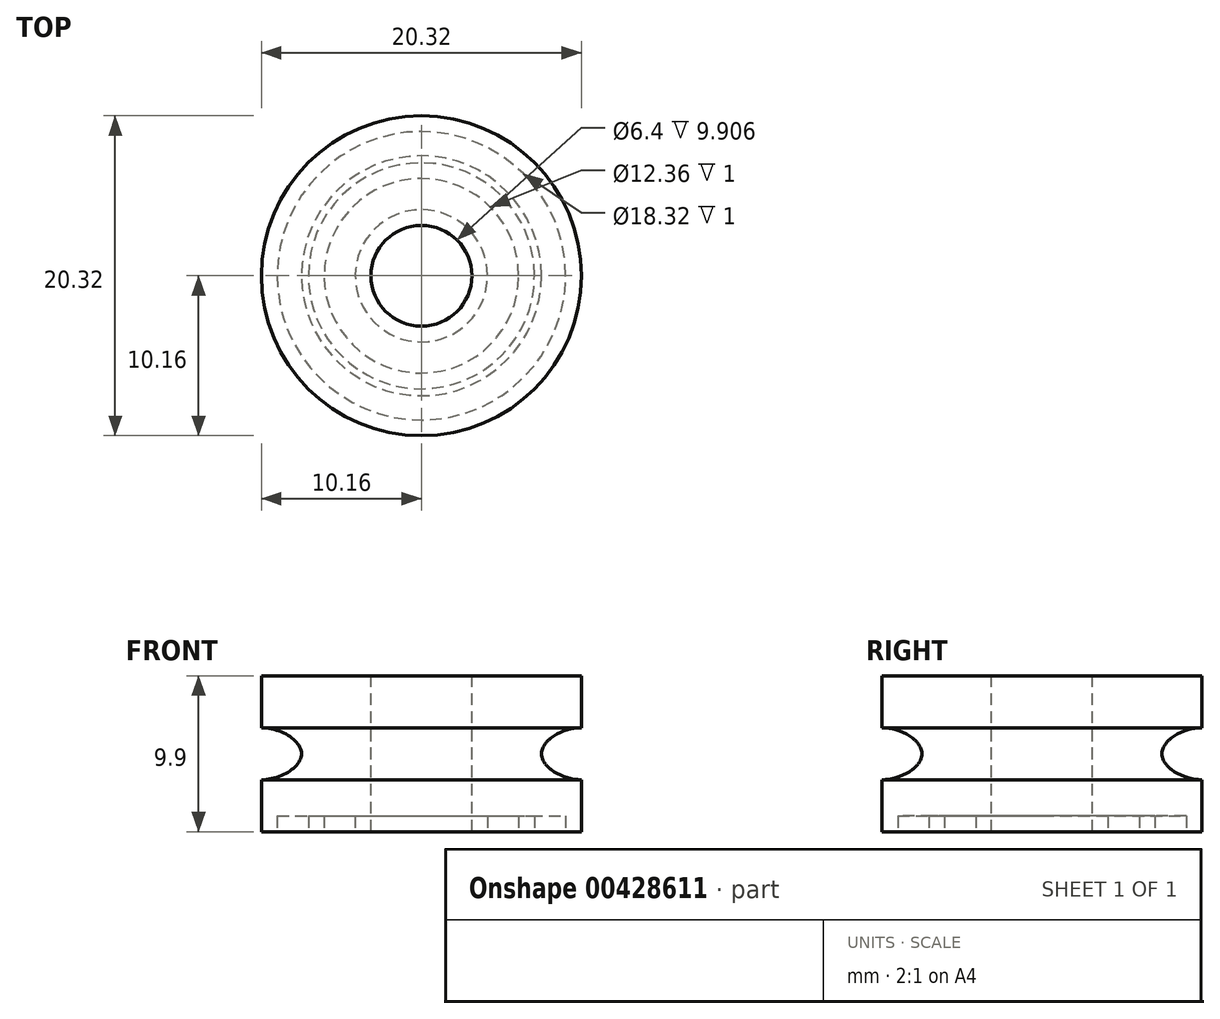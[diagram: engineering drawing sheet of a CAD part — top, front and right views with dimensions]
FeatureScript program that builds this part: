
annotation { "Feature Type Name" : "Feature", "Feature Type Description" : "" }
export const myFeature = defineFeature(function(context is Context, id is Id, definition is map)
    precondition{}
    {
        {
            var Q0;
            Q0=qCreatedBy(makeId("Front.planeOp"),FACE);
            var sketch = newSketch(context, id + "F0", { "sketchPlane" : qUnion([Q0])});
            skLineSegment(sketch, "E0", {"start": v(0, 4.95) * mm, "end": v(-10.16, 4.95) * mm});
            skLineSegment(sketch, "E1", {"start": v(-10.16, 4.95) * mm, "end": v(-10.16, 1.65) * mm});
            skLineSegment(sketch, "E2", {"start": v(-10.16, 1.65) * mm, "end": v(-7.62, 1.65) * mm});
            skLineSegment(sketch, "E3", {"start": v(-7.62, 1.65) * mm, "end": v(-7.62, 0) * mm});
            skLineSegment(sketch, "E4", {"start": v(-7.62, 0) * mm, "end": v(0, 0) * mm});
            skLineSegment(sketch, "E5", {"start": v(0, 0) * mm, "end": v(0, 4.95) * mm});
            skLineSegment(sketch, "E6", {"start": v(0, 0) * mm, "end": v(0, 25.4) * mm, "construction": true});
            skFitSpline(sketch, "E7", {"points": [v(-7.62, 0) * mm, v(-10.16, 1.65) * mm], "startDerivative": vector(0, 2.48) * mm, "endDerivative": vector(-3.81, 0) * mm});
            skSolve(sketch);
        }
        {
            var Q0;
            Q0 = qSketchRegion(id + "F0", true);
            var Q1;
            Q1=sQuery(id+"F0.wireOp",EDGE,"E6");
            revolve(context, id + "F1", {"entities" : qUnion([Q0]), "axis" : qUnion([Q1]), "revolveType" : RevolveType.FULL});
        }
        {
            var Q0;
            Q0=makeQuery(id+"F1.opRevolve","SWEPT_BODY",BODY,{"disambiguationData":[OSD([sQuery(id+"F0.wireOp",EDGE,"E0"),sQuery(id+"F0.wireOp",EDGE,"E1"),sQuery(id+"F0.wireOp",EDGE,"E2"),sQuery(id+"F0.wireOp",EDGE,"E3"),sQuery(id+"F0.wireOp",EDGE,"E4"),sQuery(id+"F0.wireOp",EDGE,"E5")])]});
            var Q1;
            Q1=qCreatedBy(makeId("Top.planeOp"),FACE);
            mirror(context, id + "F2", {"operationType" : NewBodyOperationType.ADD, "entities" : qUnion([Q0]), "mirrorPlane" : qUnion([Q1])});
        }
        {
            var Q0;
            Q0=makeQuery(id+"F1.opRevolve","SWEPT_FACE",FACE,{"disambiguationData":[OSD([sQuery(id+"F0.wireOp",EDGE,"E0")])]});
            var sketch = newSketch(context, id + "F3", { "sketchPlane" : qUnion([Q0])});
            skCircle(sketch, "E8", {"center": v(0, 0) * mm, "radius": 3.2 * mm});
            skSolve(sketch);
        }
        {
            var Q0;
            Q0 = qSketchRegion(id + "F3", true);
            extrude(context, id + "F4", {"entities" : qUnion([Q0]), "operationType" : NewBodyOperationType.REMOVE, "endBound" : BoundingType.THROUGH_ALL, "oppositeDirection" : true, "depth" : 25.4 * mm});
        }
        {
            var Q0;
            Q0=makeQuery(id+"F2.opPattern","COPY",FACE,{"derivedFrom":makeQuery(id+"F1.opRevolve","SWEPT_FACE",FACE,{"disambiguationData":[OSD([sQuery(id+"F0.wireOp",EDGE,"E0")])]}),"instanceName":"1"});
            var sketch = newSketch(context, id + "F5", { "sketchPlane" : qUnion([Q0])});
            skLineSegment(sketch, "E9", {"start": v(-3.2, 0) * mm, "end": v(-10.16, 0) * mm, "construction": true});
            skCircle(sketch, "E10", {"center": v(0, 0) * mm, "radius": 6.68 * mm, "construction": true});
            skCircle(sketch, "E11", {"center": v(0, 0) * mm, "radius": 6.18 * mm});
            skCircle(sketch, "E12", {"center": v(0, 0) * mm, "radius": 7.18 * mm});
            skCircle(sketch, "E13", {"center": v(0, 0) * mm, "radius": 9.16 * mm});
            skCircle(sketch, "E14", {"center": v(0, 0) * mm, "radius": 4.2 * mm});
            skSolve(sketch);
        }
        {
            var Q0;
            Q0=makeQuery(id+"F5.imprint","IMPRINT",FACE,{"disambiguationData":[TD([[makeQuery(id+"F5.imprint","IMPRINT",EDGE,{"derivedFrom":sQuery(id+"F5.wireOp",EDGE,"E11")}),1.0]])]});
            var Q1;
            Q1=makeQuery(id+"F5.imprint","IMPRINT",FACE,{"disambiguationData":[TD([[makeQuery(id+"F5.imprint","IMPRINT",EDGE,{"derivedFrom":sQuery(id+"F5.wireOp",EDGE,"E12")}),-1.0]])]});
            extrude(context, id + "F6", {"entities" : qUnion([Q0, Q1]), "operationType" : NewBodyOperationType.REMOVE, "oppositeDirection" : true, "depth" : 1 * mm});
        }
    });
